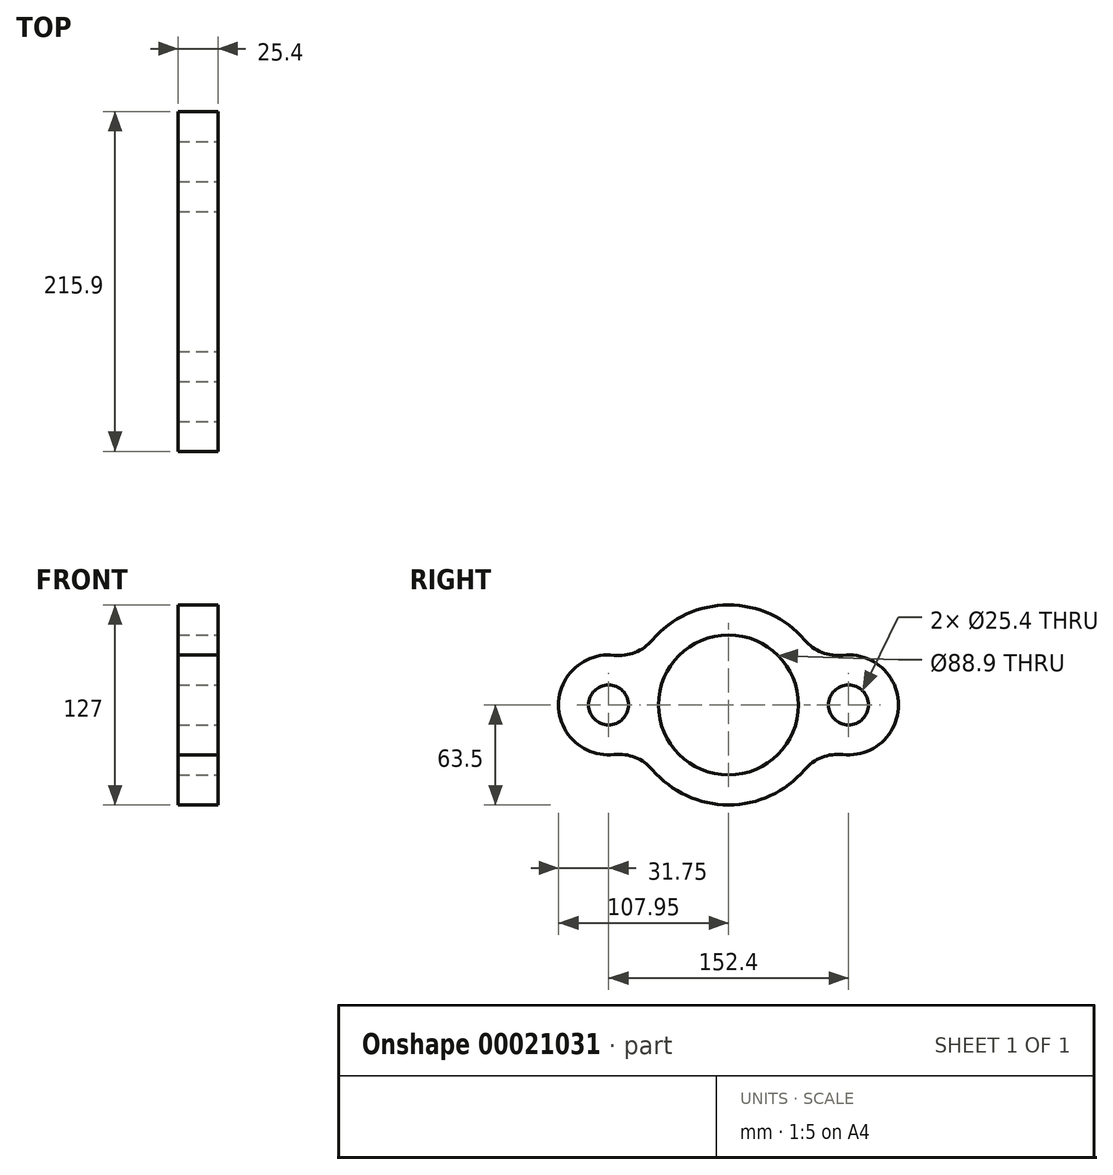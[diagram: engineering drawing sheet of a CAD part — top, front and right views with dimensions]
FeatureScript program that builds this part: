
annotation { "Feature Type Name" : "Feature", "Feature Type Description" : "" }
export const myFeature = defineFeature(function(context is Context, id is Id, definition is map)
    precondition{}
    {
        {
            var Q0;
            Q0=qCreatedBy(makeId("Right.planeOp"),FACE);
            var sketch = newSketch(context, id + "F0", { "sketchPlane" : qUnion([Q0])});
            skCircle(sketch, "E0", {"center": v(0, 0) * mm, "radius": 44.45 * mm});
            skCircle(sketch, "E1", {"center": v(-76.2, 0) * mm, "radius": 12.7 * mm});
            skCircle(sketch, "E2", {"center": v(76.2, 0) * mm, "radius": 12.7 * mm});
            skCircle(sketch, "E3", {"center": v(-76.2, 0) * mm, "radius": 31.75 * mm});
            skCircle(sketch, "E4", {"center": v(76.2, 0) * mm, "radius": 31.75 * mm});
            skCircle(sketch, "E5", {"center": v(0, 0) * mm, "radius": 63.5 * mm});
            skArc(sketch, "E6", {"start": v(-72.7, 31.56) * mm, "mid": v(-59.3, 33.35) * mm, "end": v(-48.32, 41.2) * mm});
            skArc(sketch, "E7", {"start": v(48.32, 41.2) * mm, "mid": v(59.3, 33.35) * mm, "end": v(72.7, 31.56) * mm});
            skArc(sketch, "E8", {"start": v(-48.32, -41.2) * mm, "mid": v(-59.3, -33.35) * mm, "end": v(-72.7, -31.56) * mm});
            skArc(sketch, "E9", {"start": v(72.7, -31.56) * mm, "mid": v(59.3, -33.35) * mm, "end": v(48.32, -41.2) * mm});
            skSolve(sketch);
        }
        {
            var Q0;
            Q0 = qSketchRegion(id + "F0", true);
            var Q1;
            {var subQ1=sQuery(id+"F0.wireOp",EDGE,"E3");var subQ5=makeQuery(id+"F0.imprint","INTERSECT",VERTEX,{"derivedFrom":[sQuery(id+"F0.wireOp",EDGE,"E0"),subQ1]});Q1=makeQuery(id+"F0.imprint","IMPRINT",FACE,{"disambiguationData":[TD([[makeQuery(id+"F0.imprint","IMPRINT",EDGE,{"disambiguationData":[TD([[subQ5,-1.0]])],"derivedFrom":subQ1}),1.0]])]});}
            var Q2;
            {var subQ1=sQuery(id+"F0.wireOp",EDGE,"E4");var subQ5=makeQuery(id+"F0.imprint","INTERSECT",VERTEX,{"derivedFrom":[sQuery(id+"F0.wireOp",EDGE,"E0"),subQ1]});Q2=makeQuery(id+"F0.imprint","IMPRINT",FACE,{"disambiguationData":[TD([[makeQuery(id+"F0.imprint","IMPRINT",EDGE,{"disambiguationData":[TD([[subQ5,1.0]])],"derivedFrom":subQ1}),1.0]])]});}
            extrude(context, id + "F1", {"entities" : qUnion([Q0, Q1, Q2]), "oppositeDirection" : true, "depth" : 25.4 * mm});
        }
    });
